# Revit family: 1121xxx Mashiko 400 Round
name_source: partatom
category: Lighting Fixtures
units: mm (PartAtom-declared; Revit-internal decimal feet)

## family parameters
Always vertical = Yes
Cut with Voids When Loaded = No
Host = Ceiling
Light Source = No
OmniClass Number = 23.80.70.11
OmniClass Title = Luminaries for Internal Lighting
Part Type = Normal
Room Calculation Point = No
Round Connector Dimension = Use Diameter
Shared = No

## types (2) — shared parameters
Dimmable = Yes
Dimming Method = Lamp Dependent
Driver Included = Not Applicable
Driver Required = No
Efficacy (lm/w) = Lamp Dependent
Light Source Fixed = No
Main Finish = Polished Chrome
Main Material = Metal - Stainless Steel
Manufacturer URL - Europe and Rest of World = www.astrolighting.com
Manufacturer URL - North America = us.astrolighting.com
Power (Watts) = Lamp Dependent
Product CCT = Lamp Dependent
Product CRI = Lamp Dependent
Product Dimensions (MM) = 100x400x400
Product Location = Bathroom
Product Name = Mashiko 400 Round
Product SKU = 1121031
Product URL = https://us.astrolighting.com
Product Weight (KG) = 3 mm  [stored 0.00984252 ft]
zero-valued in all types: Default Elevation

## per-type parameters (varying)
| type | ADA compliant | Electrical Class | Lamp | Location / IP Rating |
| Mashiko 400 Round cETLus | Yes - see datasheet | 1 | 3x 43W max E26 med | Damp |
| Mashiko 400 Round CE | Not Applicable | II | 3x 42W max E27 es | IP44 |

note: [stored X ft] marks values corroborated as IEEE doubles in the binary element streams (Revit-internal decimal feet)

## geometry (parser evidence)
native form markers: Sweep x3
no freeform markers — native parametric forms only
